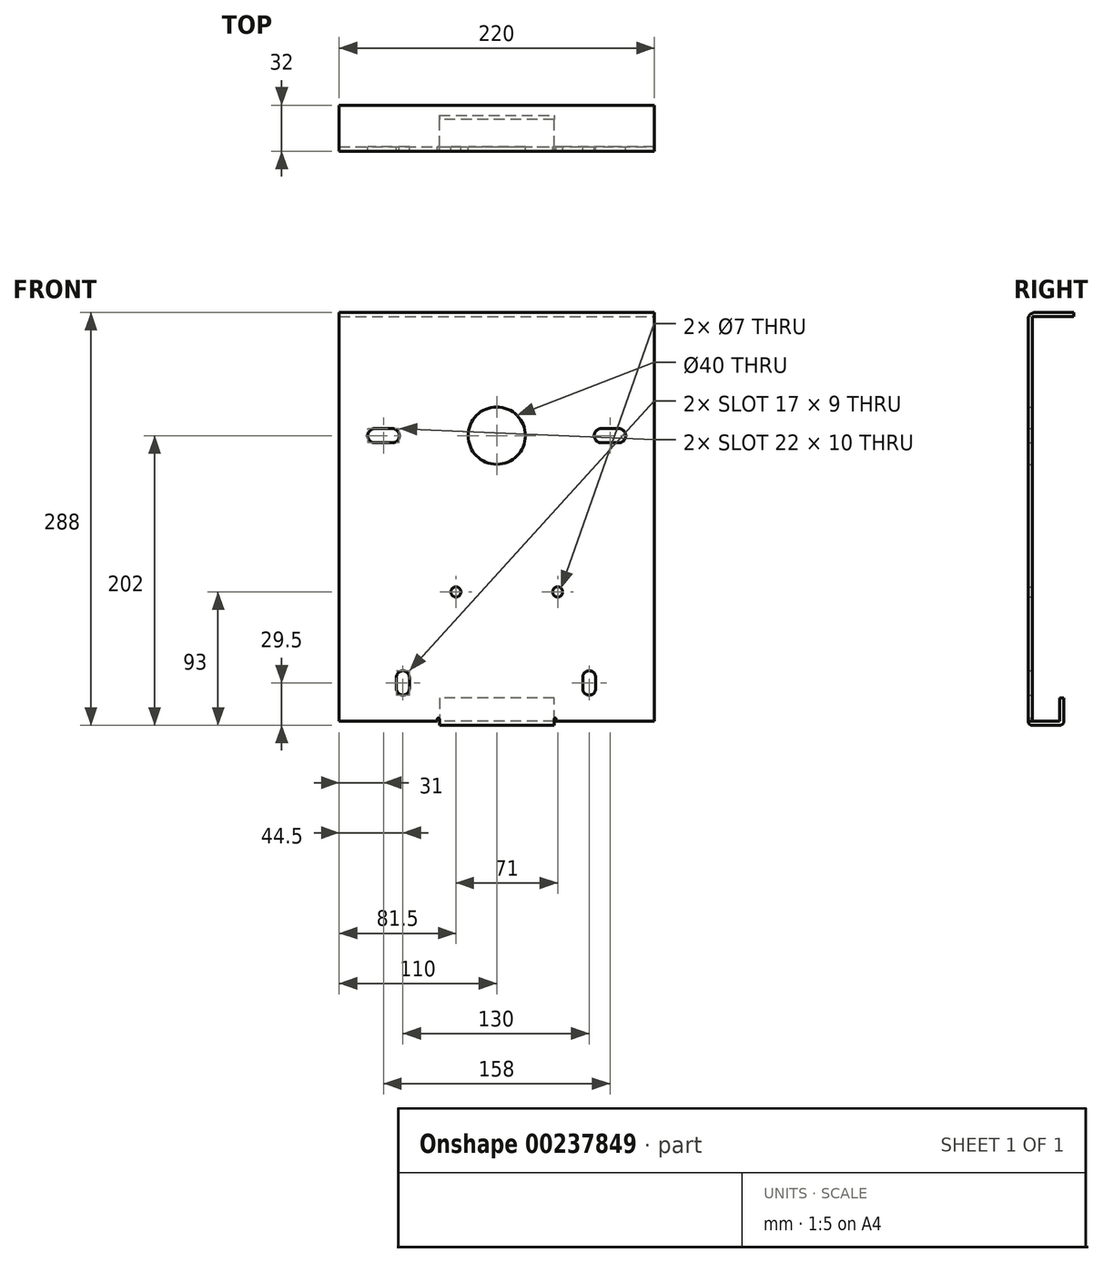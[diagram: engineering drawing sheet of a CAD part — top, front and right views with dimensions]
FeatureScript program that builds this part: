
annotation { "Feature Type Name" : "Feature", "Feature Type Description" : "" }
export const myFeature = defineFeature(function(context is Context, id is Id, definition is map)
    precondition{}
    {
        {
            var Q0;
            Q0=qCreatedBy(makeId("Front.planeOp"),FACE);
            var sketch = newSketch(context, id + "F0", { "sketchPlane" : qUnion([Q0])});
            skLineSegment(sketch, "E0.bottom", {"start": v(110, -142.5) * mm, "end": v(41.5, -142.5) * mm});
            skLineSegment(sketch, "E0.top", {"start": v(110, 142.5) * mm, "end": v(-110, 142.5) * mm});
            skLineSegment(sketch, "E0.left", {"start": v(110, -142.5) * mm, "end": v(110, 142.5) * mm});
            skLineSegment(sketch, "E0.right", {"start": v(-110, -142.5) * mm, "end": v(-110, 142.5) * mm});
            skPoint(sketch, "E0.middle", {"position": v(0, 0) * mm});
            skLineSegment(sketch, "E1.bottom", {"start": v(-65.5, -124.5) * mm, "end": v(-65.5, -124.5) * mm});
            skLineSegment(sketch, "E1.top", {"start": v(-65.5, -107.5) * mm, "end": v(-65.5, -107.5) * mm});
            skLineSegment(sketch, "E1.left", {"start": v(-70, -120) * mm, "end": v(-70, -112) * mm});
            skLineSegment(sketch, "E1.right", {"start": v(-61, -120) * mm, "end": v(-61, -112) * mm});
            skPoint(sketch, "E2.visualSharp", {"position": v(-61, -124.5) * mm});
            skArc(sketch, "E2.filletArc", {"start": v(-65.5, -124.5) * mm, "mid": v(-62.32, -123.18) * mm, "end": v(-61, -120) * mm});
            skPoint(sketch, "E3.visualSharp", {"position": v(-70, -107.5) * mm});
            skArc(sketch, "E3.filletArc", {"start": v(-65.5, -107.5) * mm, "mid": v(-68.68, -108.82) * mm, "end": v(-70, -112) * mm});
            skPoint(sketch, "E4.visualSharp", {"position": v(-61, -107.5) * mm});
            skArc(sketch, "E4.filletArc", {"start": v(-61, -112) * mm, "mid": v(-62.32, -108.82) * mm, "end": v(-65.5, -107.5) * mm});
            skPoint(sketch, "E5.visualSharp", {"position": v(-70, -124.5) * mm});
            skArc(sketch, "E5.filletArc", {"start": v(-70, -120) * mm, "mid": v(-68.68, -123.18) * mm, "end": v(-65.5, -124.5) * mm});
            skPoint(sketch, "E6.visualSharp", {"position": v(64.5, -107.5) * mm});
            skLineSegment(sketch, "E7.bottom", {"start": v(64.5, -107.5) * mm, "end": v(64.5, -107.5) * mm});
            skLineSegment(sketch, "E8", {"start": v(69, -112) * mm, "end": v(69, -120) * mm});
            skLineSegment(sketch, "E9", {"start": v(64.5, -124.5) * mm, "end": v(64.5, -124.5) * mm});
            skLineSegment(sketch, "E10", {"start": v(60, -120) * mm, "end": v(60, -112) * mm});
            skPoint(sketch, "E11.visualSharp", {"position": v(69, -107.5) * mm});
            skArc(sketch, "E11.filletArc", {"start": v(69, -112) * mm, "mid": v(67.68, -108.82) * mm, "end": v(64.5, -107.5) * mm});
            skPoint(sketch, "E12.visualSharp", {"position": v(69, -124.5) * mm});
            skArc(sketch, "E12.filletArc", {"start": v(64.5, -124.5) * mm, "mid": v(67.68, -123.18) * mm, "end": v(69, -120) * mm});
            skPoint(sketch, "E13.visualSharp", {"position": v(60, -124.5) * mm});
            skArc(sketch, "E13.filletArc", {"start": v(60, -120) * mm, "mid": v(61.32, -123.18) * mm, "end": v(64.5, -124.5) * mm});
            skPoint(sketch, "E14.visualSharp", {"position": v(60, -107.5) * mm});
            skArc(sketch, "E14.filletArc", {"start": v(64.5, -107.5) * mm, "mid": v(61.32, -108.82) * mm, "end": v(60, -112) * mm});
            skCircle(sketch, "E15", {"center": v(-28.5, -52.5) * mm, "radius": 3.5 * mm});
            skCircle(sketch, "E16", {"center": v(42.5, -52.5) * mm, "radius": 3.5 * mm});
            skLineSegment(sketch, "E17", {"start": v(-90, 56.5) * mm, "end": v(-90, 56.5) * mm});
            skLineSegment(sketch, "E18", {"start": v(-85, 61.5) * mm, "end": v(-73, 61.5) * mm});
            skLineSegment(sketch, "E19", {"start": v(-68, 56.5) * mm, "end": v(-68, 56.5) * mm});
            skLineSegment(sketch, "E20", {"start": v(-73, 51.5) * mm, "end": v(-85, 51.5) * mm});
            skPoint(sketch, "E21.visualSharp", {"position": v(-68, 61.5) * mm});
            skArc(sketch, "E21.filletArc", {"start": v(-68, 56.5) * mm, "mid": v(-69.46, 60.04) * mm, "end": v(-73, 61.5) * mm});
            skPoint(sketch, "E22.visualSharp", {"position": v(-68, 51.5) * mm});
            skArc(sketch, "E22.filletArc", {"start": v(-73, 51.5) * mm, "mid": v(-69.46, 52.96) * mm, "end": v(-68, 56.5) * mm});
            skPoint(sketch, "E23.visualSharp", {"position": v(-90, 51.5) * mm});
            skArc(sketch, "E23.filletArc", {"start": v(-90, 56.5) * mm, "mid": v(-88.54, 52.96) * mm, "end": v(-85, 51.5) * mm});
            skPoint(sketch, "E24.visualSharp", {"position": v(-90, 61.5) * mm});
            skArc(sketch, "E24.filletArc", {"start": v(-85, 61.5) * mm, "mid": v(-88.54, 60.04) * mm, "end": v(-90, 56.5) * mm});
            skLineSegment(sketch, "E25", {"start": v(90, 56.5) * mm, "end": v(90, 56.5) * mm});
            skLineSegment(sketch, "E26", {"start": v(85, 61.5) * mm, "end": v(73, 61.5) * mm});
            skLineSegment(sketch, "E27", {"start": v(68, 56.5) * mm, "end": v(68, 56.5) * mm});
            skLineSegment(sketch, "E28", {"start": v(73, 51.5) * mm, "end": v(85, 51.5) * mm});
            skPoint(sketch, "E29.visualSharp", {"position": v(68, 61.5) * mm});
            skArc(sketch, "E29.filletArc", {"start": v(73, 61.5) * mm, "mid": v(69.46, 60.04) * mm, "end": v(68, 56.5) * mm});
            skPoint(sketch, "E30.visualSharp", {"position": v(68, 51.5) * mm});
            skArc(sketch, "E30.filletArc", {"start": v(68, 56.5) * mm, "mid": v(69.46, 52.96) * mm, "end": v(73, 51.5) * mm});
            skPoint(sketch, "E31.visualSharp", {"position": v(90, 51.5) * mm});
            skArc(sketch, "E31.filletArc", {"start": v(85, 51.5) * mm, "mid": v(88.54, 52.96) * mm, "end": v(90, 56.5) * mm});
            skPoint(sketch, "E32.visualSharp", {"position": v(90, 61.5) * mm});
            skArc(sketch, "E32.filletArc", {"start": v(90, 56.5) * mm, "mid": v(88.54, 60.04) * mm, "end": v(85, 61.5) * mm});
            skCircle(sketch, "E33", {"center": v(0, 56.5) * mm, "radius": 20 * mm});
            skLineSegment(sketch, "E34", {"start": v(-110, -142.5) * mm, "end": v(-41.5, -142.5) * mm});
            skLineSegment(sketch, "E35", {"start": v(-40, -142.5) * mm, "end": v(-40, -145.5) * mm});
            skLineSegment(sketch, "E36", {"start": v(-40, -145.5) * mm, "end": v(40, -145.5) * mm});
            skLineSegment(sketch, "E37", {"start": v(40, -145.5) * mm, "end": v(40, -142.5) * mm});
            skLineSegment(sketch, "E38", {"start": v(-41.5, -142.5) * mm, "end": v(-41.5, -141.25) * mm});
            skLineSegment(sketch, "E39", {"start": v(-40.75, -140.5) * mm, "end": v(-40.75, -140.5) * mm});
            skLineSegment(sketch, "E40", {"start": v(-40, -141.25) * mm, "end": v(-40, -142.5) * mm});
            skPoint(sketch, "E41.visualSharp", {"position": v(-40, -140.5) * mm});
            skArc(sketch, "E41.filletArc", {"start": v(-40, -141.25) * mm, "mid": v(-40.22, -140.72) * mm, "end": v(-40.75, -140.5) * mm});
            skPoint(sketch, "E42.visualSharp", {"position": v(-41.5, -140.5) * mm});
            skArc(sketch, "E42.filletArc", {"start": v(-40.75, -140.5) * mm, "mid": v(-41.28, -140.72) * mm, "end": v(-41.5, -141.25) * mm});
            skLineSegment(sketch, "E43", {"start": v(40, -142.5) * mm, "end": v(40, -141.25) * mm});
            skLineSegment(sketch, "E44", {"start": v(40.75, -140.5) * mm, "end": v(40.75, -140.5) * mm});
            skLineSegment(sketch, "E45", {"start": v(41.5, -141.25) * mm, "end": v(41.5, -142.5) * mm});
            skPoint(sketch, "E46.visualSharp", {"position": v(40, -140.5) * mm});
            skArc(sketch, "E46.filletArc", {"start": v(40.75, -140.5) * mm, "mid": v(40.22, -140.72) * mm, "end": v(40, -141.25) * mm});
            skPoint(sketch, "E47.visualSharp", {"position": v(41.5, -140.5) * mm});
            skArc(sketch, "E47.filletArc", {"start": v(41.5, -141.25) * mm, "mid": v(41.28, -140.72) * mm, "end": v(40.75, -140.5) * mm});
            skLineSegment(sketch, "E48.trimOffspring", {"start": v(-41.5, -142.5) * mm, "end": v(-110, -142.5) * mm});
            skLineSegment(sketch, "E49", {"start": v(-110, 142.5) * mm, "end": v(-110, 139.5) * mm});
            skLineSegment(sketch, "E50", {"start": v(-110, 139.5) * mm, "end": v(110, 139.5) * mm});
            skLineSegment(sketch, "E51", {"start": v(110, 139.5) * mm, "end": v(110, 142.5) * mm});
            skLineSegment(sketch, "E52", {"start": v(-40, -142.5) * mm, "end": v(40, -142.5) * mm});
            skSolve(sketch);
        }
        {
            var Q0;
            Q0=makeQuery(id+"F0.imprint","IMPRINT",FACE,{"disambiguationData":[TD([[makeQuery(id+"F0.imprint","IMPRINT",EDGE,{"derivedFrom":sQuery(id+"F0.wireOp",EDGE,"E0.bottom")}),-1.0]])]});
            extrude(context, id + "F1", {"entities" : qUnion([Q0]), "depth" : 3 * mm});
        }
        {
            var Q0;
            Q0=makeQuery(id+"F0.imprint","IMPRINT",FACE,{"disambiguationData":[TD([[makeQuery(id+"F0.imprint","IMPRINT",EDGE,{"derivedFrom":sQuery(id+"F0.wireOp",EDGE,"E0.top")}),1.0]])]});
            extrude(context, id + "F2", {"entities" : qUnion([Q0]), "operationType" : NewBodyOperationType.ADD, "depth" : 3 * mm, "hasSecondDirection" : true, "secondDirectionOppositeDirection" : true, "secondDirectionDepth" : 29 * mm});
        }
        {
            var Q0;
            Q0=makeQuery(id+"F2.opExtrude","CAP_EDGE",EDGE,{"disambiguationData":[OSD([sQuery(id+"F0.wireOp",EDGE,"E0.top")])],"isStart":false});
            var Q1;
            Q1=makeQuery(id+"F1.opExtrude","CAP_EDGE",EDGE,{"disambiguationData":[OSD([sQuery(id+"F0.wireOp",EDGE,"E50")])],"isStart":true});
            fillet(context, id + "F3", {"entities" : qUnion([Q0, Q1]), "radius" : 5 * mm, "tangentPropagation" : true, "allowEdgeOverflow" : false});
        }
        {
            var Q0;
            Q0=makeQuery(id+"F0.imprint","IMPRINT",FACE,{"disambiguationData":[TD([[makeQuery(id+"F0.imprint","IMPRINT",EDGE,{"derivedFrom":sQuery(id+"F0.wireOp",EDGE,"E35")}),1.0]])]});
            extrude(context, id + "F4", {"entities" : qUnion([Q0]), "operationType" : NewBodyOperationType.ADD, "depth" : 3 * mm, "hasSecondDirection" : true, "secondDirectionOppositeDirection" : true, "secondDirectionDepth" : 22 * mm});
        }
        {
            var Q0;
            Q0=makeQuery(id+"F4.opExtrude","CAP_EDGE",EDGE,{"disambiguationData":[OSD([sQuery(id+"F0.wireOp",EDGE,"E36")])],"isStart":false});
            fillet(context, id + "F5", {"entities" : qUnion([Q0]), "radius" : 3 * mm, "tangentPropagation" : true, "allowEdgeOverflow" : false});
        }
        {
            var Q0;
            Q0=makeQuery(id+"F4.boolean.opBoolean","MERGE",FACE,{"derivedFrom":[makeQuery(id+"F1.opExtrude","SWEPT_FACE",FACE,{"disambiguationData":[OSD([sQuery(id+"F0.wireOp",EDGE,"E40")])]}),makeQuery(id+"F4.opExtrude","SWEPT_FACE",FACE,{"disambiguationData":[OSD([sQuery(id+"F0.wireOp",EDGE,"E35")])]})]});
            var sketch = newSketch(context, id + "F6", { "sketchPlane" : qUnion([Q0])});
            skLineSegment(sketch, "E53", {"start": v(-22, -142.5) * mm, "end": v(-22, -126.5) * mm});
            skLineSegment(sketch, "E54", {"start": v(-22, -126.5) * mm, "end": v(-19, -126.5) * mm});
            skLineSegment(sketch, "E55", {"start": v(-19, -126.5) * mm, "end": v(-19, -142.5) * mm});
            skSolve(sketch);
        }
        {
            var Q0;
            Q0 = qSketchRegion(id + "F6", true);
            var Q1;
            {var subQ0=sQuery(id+"F6.wireOp",EDGE,"E53");Q1=makeQuery(id+"F6.imprint","IMPRINT",FACE,{"disambiguationData":[TD([[makeQuery(id+"F6.imprint","IMPRINT",EDGE,{"derivedFrom":subQ0}),-1.0]])]});}
            extrude(context, id + "F7", {"entities" : qUnion([Q0, Q1]), "operationType" : NewBodyOperationType.ADD, "oppositeDirection" : true, "depth" : 80 * mm});
        }
        {
            var Q0;
            Q0=makeQuery(id+"F4.opExtrude","CAP_EDGE",EDGE,{"disambiguationData":[OSD([sQuery(id+"F0.wireOp",EDGE,"E36")])],"isStart":true});
            var Q1;
            Q1=makeQuery(id+"F7.opExtrude","SWEPT_EDGE",EDGE,{"disambiguationData":[OSD([sQuery(id+"F0.wireOp",EDGE,"E35"),sQuery(id+"F0.wireOp",EDGE,"E40"),sQuery(id+"F0.wireOp",EDGE,"E52"),sQuery(id+"F6.wireOp",EDGE,"E55")])]});
            fillet(context, id + "F8", {"entities" : qUnion([Q0, Q1]), "radius" : 3 * mm, "tangentPropagation" : true, "allowEdgeOverflow" : false});
        }
    });
